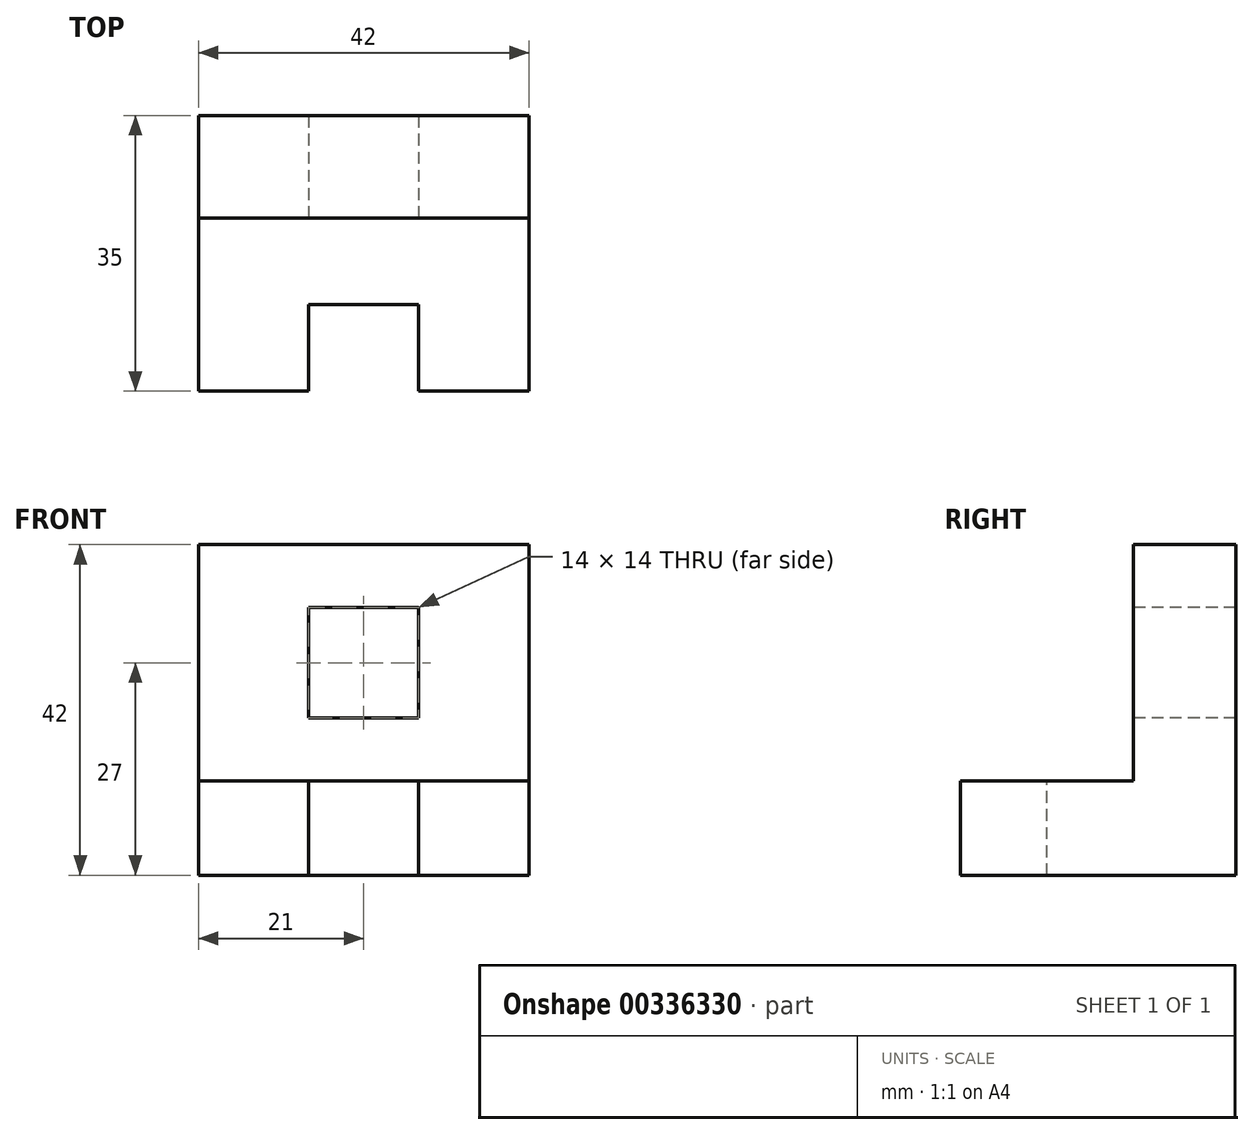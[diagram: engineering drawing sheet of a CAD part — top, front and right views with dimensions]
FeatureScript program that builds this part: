
annotation { "Feature Type Name" : "Feature", "Feature Type Description" : "" }
export const myFeature = defineFeature(function(context is Context, id is Id, definition is map)
    precondition{}
    {
        {
            var Q0;
            Q0=qCreatedBy(makeId("Top.planeOp"),FACE);
            var sketch = newSketch(context, id + "F0", { "sketchPlane" : qUnion([Q0])});
            skLineSegment(sketch, "E0.bottom", {"start": v(0, 0) * mm, "end": v(42, 0) * mm});
            skLineSegment(sketch, "E0.top", {"start": v(0, 35) * mm, "end": v(42, 35) * mm});
            skLineSegment(sketch, "E0.left", {"start": v(0, 0) * mm, "end": v(0, 35) * mm});
            skLineSegment(sketch, "E0.right", {"start": v(42, 0) * mm, "end": v(42, 35) * mm});
            skSolve(sketch);
        }
        {
            var Q0;
            Q0 = qSketchRegion(id + "F0", true);
            extrude(context, id + "F1", {"entities" : qUnion([Q0]), "depth" : 42 * mm});
        }
        {
            var Q0;
            Q0=makeQuery(id+"F1.opExtrude","CAP_FACE",FACE,{"disambiguationData":[OSD([sQuery(id+"F0.wireOp",EDGE,"E0.bottom"),sQuery(id+"F0.wireOp",EDGE,"E0.top"),sQuery(id+"F0.wireOp",EDGE,"E0.left"),sQuery(id+"F0.wireOp",EDGE,"E0.right")])],"isStart":false});
            var sketch = newSketch(context, id + "F2", { "sketchPlane" : qUnion([Q0])});
            skLineSegment(sketch, "E1.bottom", {"start": v(0, 0) * mm, "end": v(42, 0) * mm});
            skLineSegment(sketch, "E1.top", {"start": v(0, 22) * mm, "end": v(42, 22) * mm});
            skLineSegment(sketch, "E1.left", {"start": v(0, 0) * mm, "end": v(0, 22) * mm});
            skLineSegment(sketch, "E1.right", {"start": v(42, 0) * mm, "end": v(42, 22) * mm});
            skSolve(sketch);
        }
        {
            var Q0;
            Q0 = qSketchRegion(id + "F2", true);
            extrude(context, id + "F3", {"entities" : qUnion([Q0]), "operationType" : NewBodyOperationType.REMOVE, "oppositeDirection" : true, "depth" : 30 * mm});
        }
        {
            var Q0;
            Q0=makeQuery(id+"F3.boolean.opBoolean","COPY",FACE,{"derivedFrom":makeQuery(id+"F3.opExtrude","CAP_FACE",FACE,{"disambiguationData":[OSD([sQuery(id+"F2.wireOp",EDGE,"E1.bottom"),sQuery(id+"F2.wireOp",EDGE,"E1.top"),sQuery(id+"F2.wireOp",EDGE,"E1.left"),sQuery(id+"F2.wireOp",EDGE,"E1.right")])],"isStart":false})});
            var sketch = newSketch(context, id + "F4", { "sketchPlane" : qUnion([Q0])});
            skLineSegment(sketch, "E2.bottom", {"start": v(14, 0) * mm, "end": v(28, 0) * mm});
            skLineSegment(sketch, "E2.top", {"start": v(14, 11) * mm, "end": v(28, 11) * mm});
            skLineSegment(sketch, "E2.left", {"start": v(14, 0) * mm, "end": v(14, 11) * mm});
            skLineSegment(sketch, "E2.right", {"start": v(28, 0) * mm, "end": v(28, 11) * mm});
            skSolve(sketch);
        }
        {
            var Q0;
            Q0 = qSketchRegion(id + "F4", true);
            extrude(context, id + "F5", {"entities" : qUnion([Q0]), "operationType" : NewBodyOperationType.REMOVE, "endBound" : BoundingType.THROUGH_ALL, "oppositeDirection" : true, "depth" : 25 * mm});
        }
        {
            var Q0;
            Q0=makeQuery(id+"F3.boolean.opBoolean","COPY",FACE,{"derivedFrom":makeQuery(id+"F3.opExtrude","SWEPT_FACE",FACE,{"disambiguationData":[OSD([sQuery(id+"F2.wireOp",EDGE,"E1.top")])]})});
            var sketch = newSketch(context, id + "F6", { "sketchPlane" : qUnion([Q0])});
            skLineSegment(sketch, "E3.bottom", {"start": v(14, 34) * mm, "end": v(28, 34) * mm});
            skLineSegment(sketch, "E3.top", {"start": v(14, 20) * mm, "end": v(28, 20) * mm});
            skLineSegment(sketch, "E3.left", {"start": v(14, 34) * mm, "end": v(14, 20) * mm});
            skLineSegment(sketch, "E3.right", {"start": v(28, 34) * mm, "end": v(28, 20) * mm});
            skPoint(sketch, "E3.middle", {"position": v(21, 27) * mm});
            skPoint(sketch, "E3.middle.positionSnap0", {"position": v(0, 27) * mm});
            skPoint(sketch, "E3.middle.positionSnap1", {"position": v(21, 42) * mm});
            skPoint(sketch, "E3.centerSnap0", {"position": v(0, 27) * mm});
            skPoint(sketch, "E3.centerSnap1", {"position": v(21, 42) * mm});
            skSolve(sketch);
        }
        {
            var Q0;
            Q0 = qSketchRegion(id + "F6", true);
            extrude(context, id + "F7", {"entities" : qUnion([Q0]), "operationType" : NewBodyOperationType.REMOVE, "endBound" : BoundingType.THROUGH_ALL, "oppositeDirection" : true, "depth" : 25 * mm});
        }
    });
